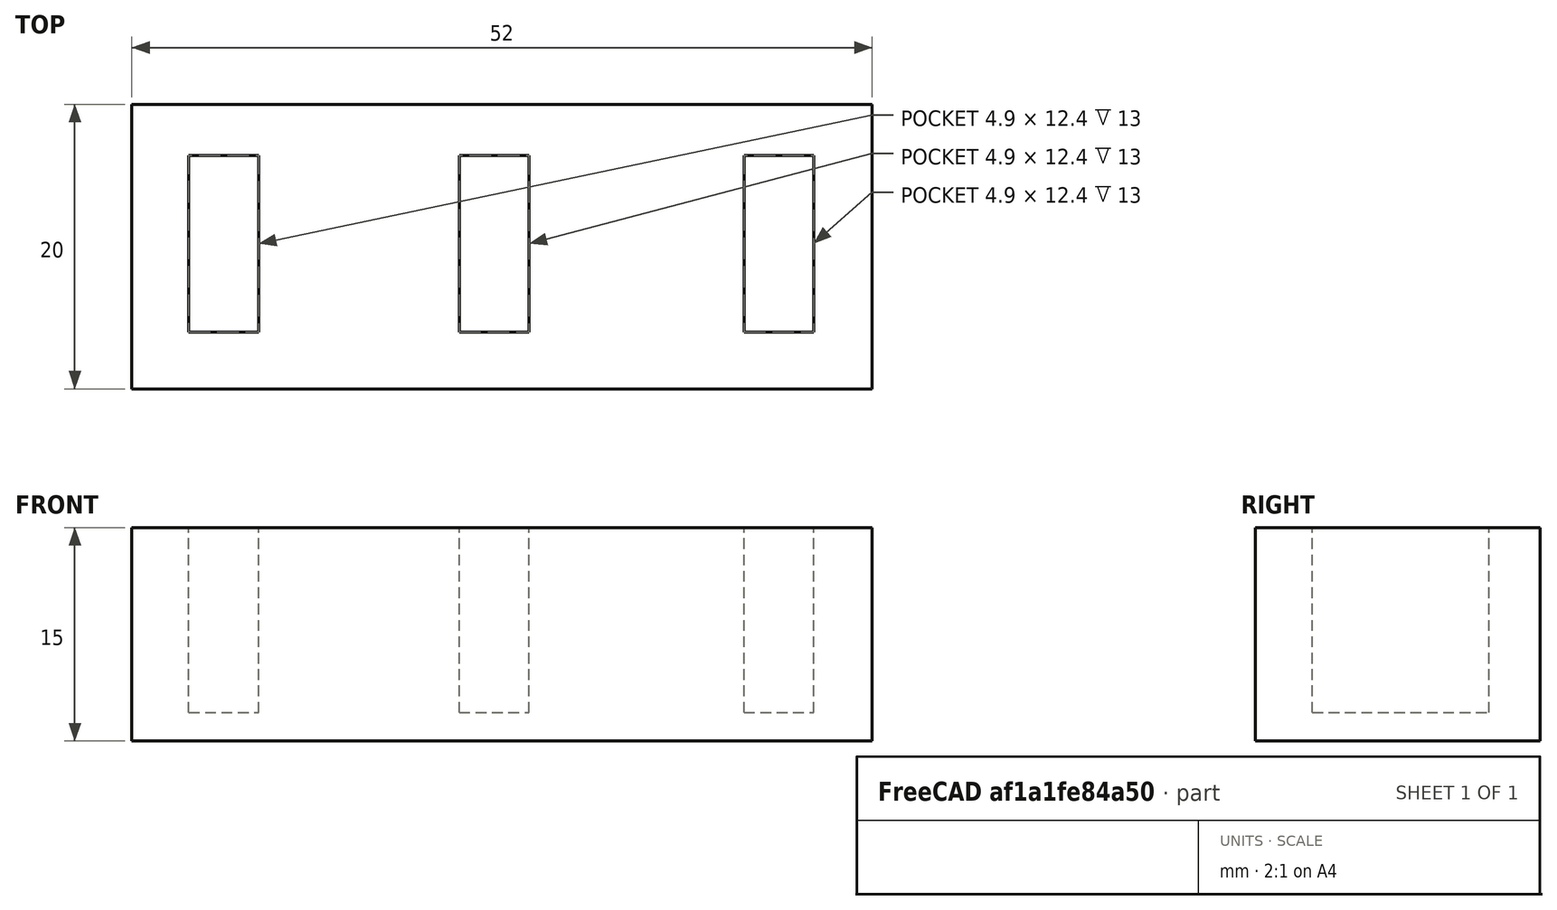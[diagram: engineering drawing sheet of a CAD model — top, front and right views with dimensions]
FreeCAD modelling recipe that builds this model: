
FCSTD DOCUMENT  (FreeCAD 0.19R)
Label: Reto 4
License: All rights reserved
LicenseURL: http://en.wikipedia.org/wiki/All_rights_reserved
objects: App::MeasureDistance×6, Part::Box×4, Part::Cut×3
note: 7 computed .brp shape members not serialized (recipe doc carries the construction recipe); baked Part::Feature solids carry a one-line shape summary decoded from their .brp

FEATURE [Part::Box] Box  label="Base"
  AttacherType = Attacher::AttachEngine3D
  Height = 15
  Length = 52
  Width = 20
FEATURE [Part::Box] Box001  label="Taladro 1"
  AttacherType = Attacher::AttachEngine3D
  Height = 25
  Length = 4.9
  Placement = pos=(4,4,2) rot=(0,0,1;0rad)
  Width = 12.4
FEATURE [Part::Box] Box002  label="Taladro 2"
  AttacherType = Attacher::AttachEngine3D
  Height = 25
  Length = 4.9
  Placement = pos=(43,4,2) rot=(0,0,1;0rad)
  Width = 12.4
FEATURE [Part::Box] Box003  label="Taladro 3"
  AttacherType = Attacher::AttachEngine3D
  Height = 25
  Length = 4.9
  Placement = pos=(23,4,2) rot=(0,0,1;0rad)
  Width = 12.4
FEATURE [Part::Cut] Cut
  Base = -> Box
  Refine = true
  Tool = -> Box001
FEATURE [Part::Cut] Cut001
  Base = -> Cut
  Refine = true
  Tool = -> Box002
FEATURE [App::MeasureDistance] Distance  label="Distance: 52,00 mm"
  Distance = 52
  P1 = (0,20,15)
  P2 = (52,20,15)
FEATURE [App::MeasureDistance] Distance001  label="Distance: 14,11 mm"
  Distance = 14.1068
  P1 = (8.9,16.044,15)
  P2 = (23,15.6075,15)
FEATURE [App::MeasureDistance] Distance002  label="Distance: 4,90 mm"
  Distance = 4.9
  P1 = (23,4,15)
  P2 = (27.9,4,15)
FEATURE [App::MeasureDistance] Distance003  label="Distance: 12,40 mm"
  Distance = 12.4
  P1 = (43,16.4,15)
  P2 = (43,4,15)
FEATURE [App::MeasureDistance] Distance004  label="Distance: 15,00 mm"
  Distance = 15
  P1 = (0,0,15)
  P2 = (0,0,0)
FEATURE [Part::Cut] Cut002  label="Reto 4"
  Base = -> Cut001
  Refine = true
  Tool = -> Box003
FEATURE [App::MeasureDistance] Distance005  label="Distance: 20,00 mm"
  Distance = 20
  P1 = (52,0,15)
  P2 = (52,20,15)
